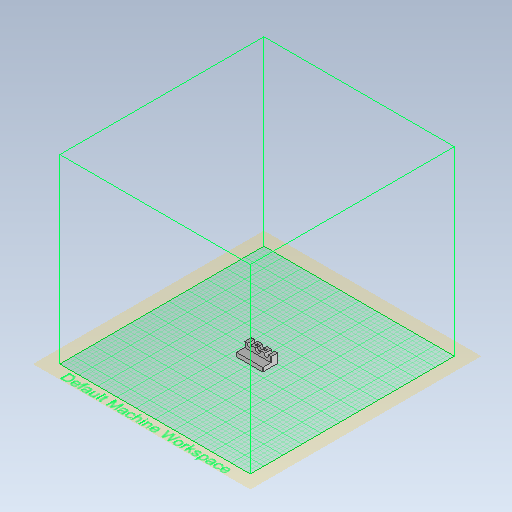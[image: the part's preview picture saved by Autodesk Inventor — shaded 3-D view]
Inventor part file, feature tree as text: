
AUTODESK INVENTOR PART (.ipt)
format: ipt  version: 2021 (Build 250183000, 183)  size: 382,976 bytes
history: native  units: in
note: dims shown in document units (in); Inventor stores cm internally (conversion verified against a paired STEP export)
features: sketch x6, extrude x5, projected_geometry x5, fillet x3
ambient origin geometry x8: Origin, YZ Plane, XZ Plane, XY Plane, X Axis, Y Axis, Z Axis, Center Point
bodies: Solid1 (feature_tree)
feature tree (19):
  extrude  "Extrusion1"  Depth=0.7874in
  extrude  "Extrusion2"  Depth=0.5906in
  sketch  "Sketch4"  dims[d5=0.3248in d6=1.4921in]
  sketch  "Sketch5"  dims[d7=0.0886in d8=0.0in d9=0.0in]
  extrude  "Extrusion3"  Depth=1.4921in
  extrude  "Extrusion4"  TaperAngle=0.0deg  [1 undecoded]
  extrude  "Extrusion5"  Depth=0.3937in
  fillet  "Fillet4"  Radius=0.8819in
  fillet  "Fillet5"  Radius=0.1772in
  fillet  "Fillet6"  Radius=0.3937in
  sketch  "Sketch1"  dims[d0=2.2835in d1=0.7874in]
  sketch  "Sketch3"  dims[d2=0.5906in d3=0.0in d4=0.3248in]
  projected_geometry  "Projected Loop2"
  projected_geometry  "Projected Loop3"
  projected_geometry  "Projected Loop4"
  sketch  "Sketch6"  dims[d10=0.8858in d11=0.2165in d12=0.8819in d13=0.1772in d14=0.3937in d15=0.0in]
  projected_geometry  "Projected Loop5"
  sketch  "Sketch8"  dims[d16=0.4134in d17=0.0in d18=0.0in d19=0.3543in d20=1.3504in d21=0.0in d25=0.0394in d26=0.0394in d27=0.0197in d28=0.0197in d29=0.0344in d30=0.0197in d31=0.0344in]
  projected_geometry  "Projected Loop7"
note: 1 required parameter value undecoded (feature->parameter linkage not recoverable at this tier; creation-order binding heuristic only, values carry confidence <= 0.55)
